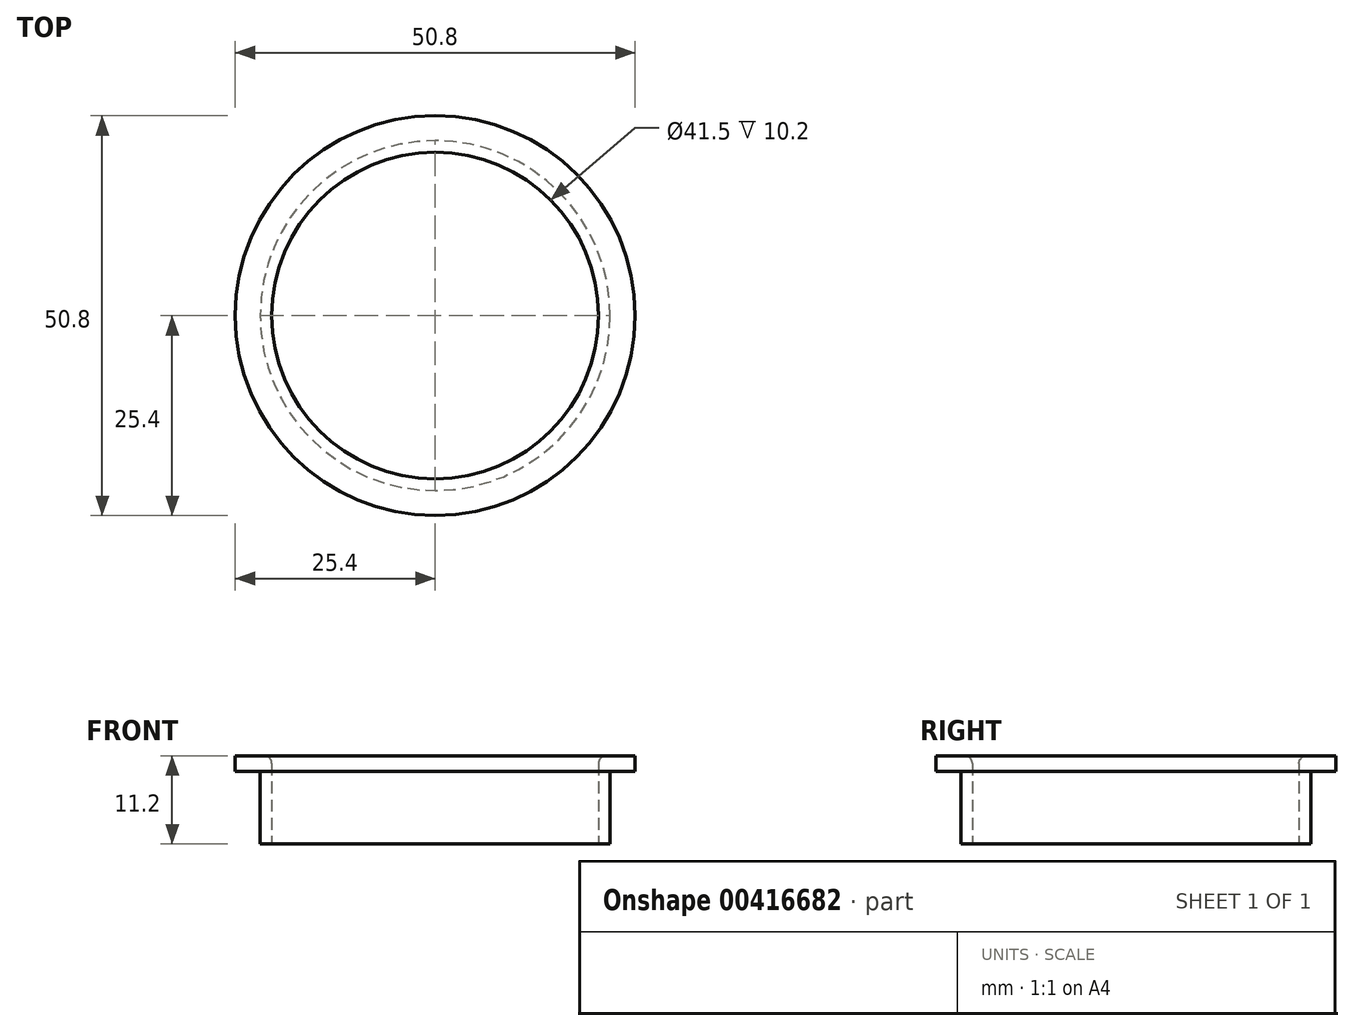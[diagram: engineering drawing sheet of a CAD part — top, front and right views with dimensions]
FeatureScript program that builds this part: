
annotation { "Feature Type Name" : "Feature", "Feature Type Description" : "" }
export const myFeature = defineFeature(function(context is Context, id is Id, definition is map)
    precondition{}
    {
        {
            var Q0;
            Q0=qCreatedBy(makeId("Top.planeOp"),FACE);
            var sketch = newSketch(context, id + "F0", { "sketchPlane" : qUnion([Q0])});
            skCircle(sketch, "E0", {"center": v(0, 0) * mm, "radius": 22.23 * mm});
            skSolve(sketch);
        }
        {
            var Q0;
            Q0=makeQuery(id+"F0.imprint","IMPRINT",FACE,{"disambiguationData":[TD([[makeQuery(id+"F0.imprint","IMPRINT",EDGE,{"derivedFrom":sQuery(id+"F0.wireOp",EDGE,"E0")}),1.0]])]});
            extrude(context, id + "F1", {"entities" : qUnion([Q0]), "depth" : 11.2 * mm});
        }
        {
            var Q0;
            Q0=makeQuery(id+"F1.opExtrude","CAP_FACE",FACE,{"disambiguationData":[OSD([sQuery(id+"F0.wireOp",EDGE,"E0")])],"isStart":false});
            var sketch = newSketch(context, id + "F2", { "sketchPlane" : qUnion([Q0])});
            skCircle(sketch, "E1", {"center": v(0, 0) * mm, "radius": 25.4 * mm});
            skSolve(sketch);
        }
        {
            var Q0;
            Q0=makeQuery(id+"F2.imprint","IMPRINT",FACE,{"disambiguationData":[TD([[makeQuery(id+"F2.imprint","IMPRINT",EDGE,{"derivedFrom":sQuery(id+"F2.wireOp",EDGE,"E1")}),1.0]])]});
            extrude(context, id + "F3", {"entities" : qUnion([Q0]), "operationType" : NewBodyOperationType.ADD, "oppositeDirection" : true, "depth" : 2 * mm});
        }
        {
            var Q0;
            Q0=makeQuery(id+"F1.opExtrude","CAP_FACE",FACE,{"disambiguationData":[OSD([sQuery(id+"F0.wireOp",EDGE,"E0")])],"isStart":true});
            var sketch = newSketch(context, id + "F4", { "sketchPlane" : qUnion([Q0])});
            skCircle(sketch, "E2", {"center": v(0, 0) * mm, "radius": 20.75 * mm});
            skSolve(sketch);
        }
        {
            var Q0;
            Q0=makeQuery(id+"F4.imprint","IMPRINT",FACE,{"disambiguationData":[TD([[makeQuery(id+"F4.imprint","IMPRINT",EDGE,{"derivedFrom":sQuery(id+"F4.wireOp",EDGE,"E2")}),1.0]])]});
            extrude(context, id + "F5", {"entities" : qUnion([Q0]), "operationType" : NewBodyOperationType.REMOVE, "oppositeDirection" : true, "depth" : 25 * mm});
        }
        {
            var Q0;
            {var subQ0=sQuery(id+"F0.wireOp",EDGE,"E0");Q0=makeQuery(id+"F5.boolean.opBoolean","INTERSECT",EDGE,{"derivedFrom":[makeQuery(id+"F3.boolean.opBoolean","MERGE",FACE,{"derivedFrom":[makeQuery(id+"F1.opExtrude","CAP_FACE",FACE,{"disambiguationData":[OSD([subQ0])],"isStart":false}),makeQuery(id+"F3.opExtrude","CAP_FACE",FACE,{"disambiguationData":[OSD([subQ0,sQuery(id+"F2.wireOp",EDGE,"E1")])],"isStart":true})]}),makeQuery(id+"F5.opExtrude","SWEPT_FACE",FACE,{"disambiguationData":[OSD([sQuery(id+"F4.wireOp",EDGE,"E2")])]})]});}
            fillet(context, id + "F6", {"entities" : qUnion([Q0]), "radius" : 1 * mm, "tangentPropagation" : true, "allowEdgeOverflow" : false});
        }
    });
